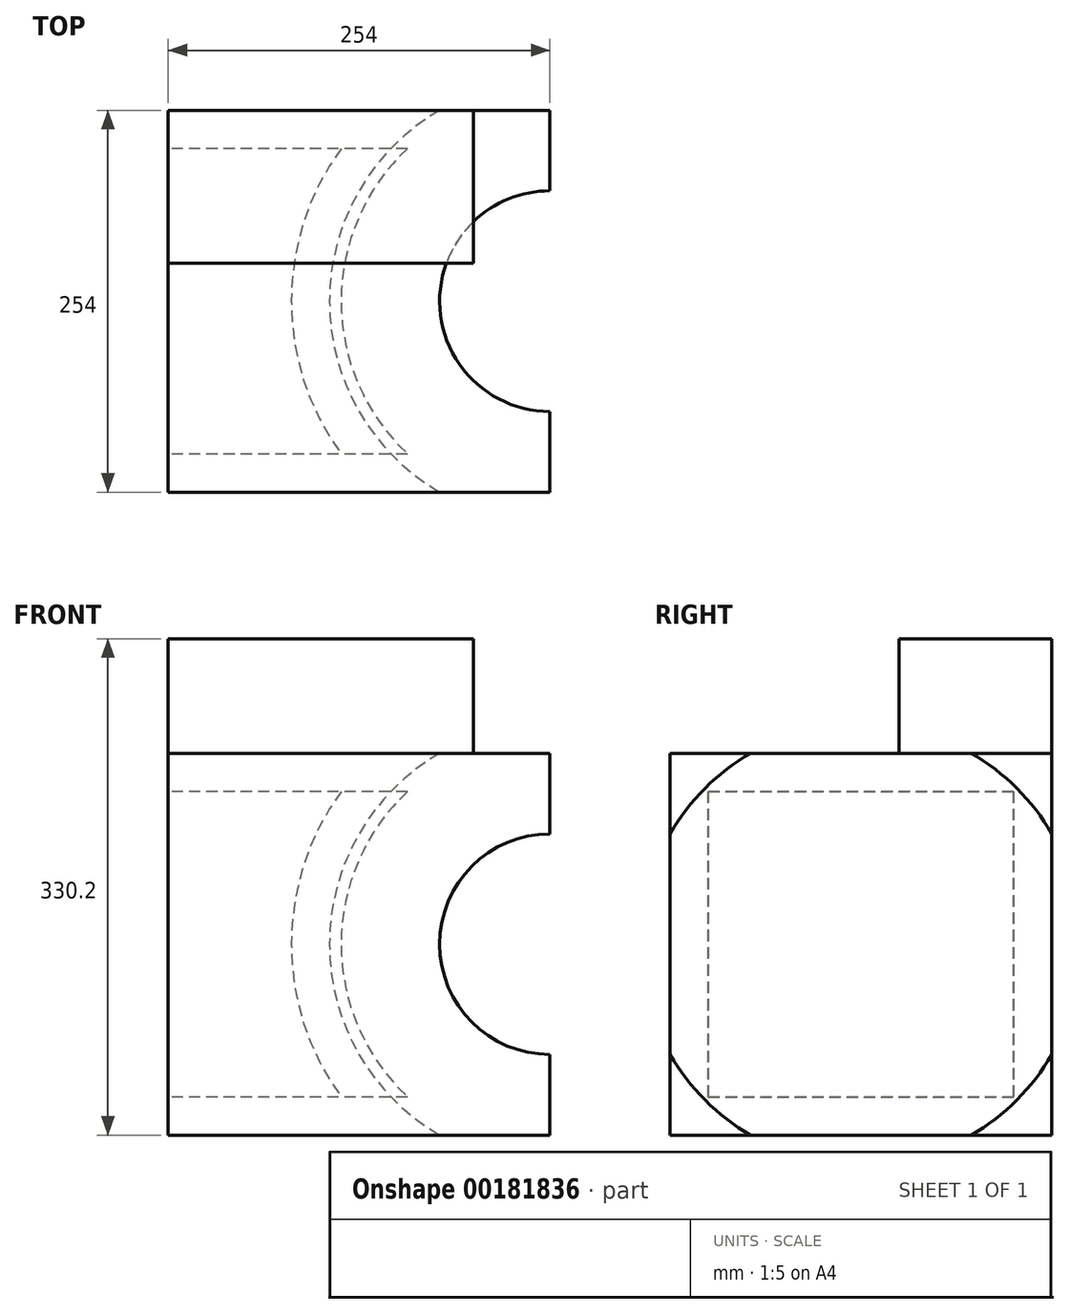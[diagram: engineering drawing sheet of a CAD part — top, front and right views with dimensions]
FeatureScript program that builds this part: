
annotation { "Feature Type Name" : "Feature", "Feature Type Description" : "" }
export const myFeature = defineFeature(function(context is Context, id is Id, definition is map)
    precondition{}
    {
        {
            var Q0;
            Q0=qCreatedBy(makeId("Right.planeOp"),FACE);
            var sketch = newSketch(context, id + "F0", { "sketchPlane" : qUnion([Q0])});
            skLineSegment(sketch, "E0.bottom", {"start": v(-254, 0) * mm, "end": v(0, 0) * mm});
            skLineSegment(sketch, "E0.top", {"start": v(-254, -254) * mm, "end": v(0, -254) * mm});
            skLineSegment(sketch, "E0.left", {"start": v(-254, 0) * mm, "end": v(-254, -254) * mm});
            skLineSegment(sketch, "E0.right", {"start": v(0, 0) * mm, "end": v(0, -254) * mm});
            skSolve(sketch);
        }
        {
            var Q0;
            Q0 = qSketchRegion(id + "F0", true);
            extrude(context, id + "F1", {"entities" : qUnion([Q0]), "depth" : 254 * mm});
        }
        {
            var Q0;
            Q0=makeQuery(id+"F1.opExtrude","CAP_FACE",FACE,{"disambiguationData":[OSD([sQuery(id+"F0.wireOp",EDGE,"E0.bottom"),sQuery(id+"F0.wireOp",EDGE,"E0.top"),sQuery(id+"F0.wireOp",EDGE,"E0.left"),sQuery(id+"F0.wireOp",EDGE,"E0.right")])],"isStart":false});
            var sketch = newSketch(context, id + "F2", { "sketchPlane" : qUnion([Q0])});
            skArc(sketch, "E1", {"start": v(19.67, -127) * mm, "mid": v(-127, 19.67) * mm, "end": v(-273.67, -127) * mm});
            skPoint(sketch, "E1.centerSnap0", {"position": v(-127, -254) * mm});
            skPoint(sketch, "E1.centerSnap1", {"position": v(0, -127) * mm});
            skLineSegment(sketch, "E2", {"start": v(19.67, -127) * mm, "end": v(-273.67, -127) * mm});
            skPoint(sketch, "E2.endSnap0", {"position": v(-254, -127) * mm});
            skSolve(sketch);
        }
        {
            var Q0;
            {var subQ0=sQuery(id+"F2.wireOp",EDGE,"E1");var subQ1=makeQuery(id+"F1.opExtrude","CAP_EDGE",EDGE,{"disambiguationData":[OSD([sQuery(id+"F0.wireOp",EDGE,"E0.bottom")])],"isStart":false});var subQ2=makeQuery(id+"F2.imprint","INTERSECT",VERTEX,{"disambiguationData":[OD(0.0)],"derivedFrom":[subQ1,subQ0]});Q0=makeQuery(id+"F2.imprint","IMPRINT",FACE,{"disambiguationData":[TD([[makeQuery(id+"F2.imprint","IMPRINT",EDGE,{"disambiguationData":[TD([[subQ2,-1.0]])],"derivedFrom":subQ0}),1.0]])]});}
            var Q1;
            {var subQ1=makeQuery(id+"F1.opExtrude","CAP_EDGE",EDGE,{"disambiguationData":[OSD([sQuery(id+"F0.wireOp",EDGE,"E0.right")])],"isStart":false});var subQ5=sQuery(id+"F2.wireOp",EDGE,"E1");var subQ10=makeQuery(id+"F2.imprint","INTERSECT",VERTEX,{"derivedFrom":[subQ1,subQ5]});Q1=makeQuery(id+"F2.imprint","IMPRINT",FACE,{"disambiguationData":[TD([[makeQuery(id+"F2.imprint","IMPRINT",EDGE,{"disambiguationData":[TD([[subQ10,-1.0]])],"derivedFrom":subQ5}),1.0]])]});}
            var Q2;
            {var subQ0=sQuery(id+"F2.wireOp",EDGE,"E2");var subQ1=sQuery(id+"F2.wireOp",EDGE,"E1");var subQ2=makeQuery(id+"F2.imprint","INTERSECT",VERTEX,{"disambiguationData":[OD(0.0)],"derivedFrom":[subQ1,subQ0]});Q2=makeQuery(id+"F2.imprint","IMPRINT",FACE,{"disambiguationData":[TD([[makeQuery(id+"F2.imprint","IMPRINT",EDGE,{"disambiguationData":[TD([[subQ2,-1.0]])],"derivedFrom":subQ1}),1.0]])]});}
            var Q3;
            {var subQ0=sQuery(id+"F2.wireOp",EDGE,"E2");var subQ1=sQuery(id+"F2.wireOp",EDGE,"E1");var subQ2=makeQuery(id+"F2.imprint","INTERSECT",VERTEX,{"disambiguationData":[OD(1.0)],"derivedFrom":[subQ1,subQ0]});Q3=makeQuery(id+"F2.imprint","IMPRINT",FACE,{"disambiguationData":[TD([[makeQuery(id+"F2.imprint","IMPRINT",EDGE,{"disambiguationData":[TD([[subQ2,1.0]])],"derivedFrom":subQ1}),1.0]])]});}
            var Q4;
            Q4=sQuery(id+"F2.wireOp",EDGE,"E2");
            revolve(context, id + "F3", {"operationType" : NewBodyOperationType.REMOVE, "entities" : qUnion([Q0, Q1, Q2, Q3]), "axis" : qUnion([Q4]), "revolveType" : RevolveType.FULL, "oppositeDirection" : true});
        }
        {
            var Q0;
            Q0=makeQuery(id+"F1.opExtrude","CAP_FACE",FACE,{"disambiguationData":[OSD([sQuery(id+"F0.wireOp",EDGE,"E0.bottom"),sQuery(id+"F0.wireOp",EDGE,"E0.top"),sQuery(id+"F0.wireOp",EDGE,"E0.left"),sQuery(id+"F0.wireOp",EDGE,"E0.right")])],"isStart":true});
            shell(context, id + "F4", {"entities" : qUnion([Q0]), "thickness" : 25.4 * mm});
        }
        {
            var Q0;
            Q0=qCreatedBy(makeId("Right.planeOp"),FACE);
            var sketch = newSketch(context, id + "F7", { "sketchPlane" : qUnion([Q0])});
            skLineSegment(sketch, "E3.bottom", {"start": v(-101.6, 76.2) * mm, "end": v(0, 76.2) * mm});
            skLineSegment(sketch, "E3.top", {"start": v(-101.6, 0) * mm, "end": v(0, 0) * mm});
            skLineSegment(sketch, "E3.left", {"start": v(-101.6, 76.2) * mm, "end": v(-101.6, 0) * mm});
            skLineSegment(sketch, "E3.right", {"start": v(0, 76.2) * mm, "end": v(0, 0) * mm});
            skSolve(sketch);
        }
        {
            var Q0;
            Q0 = qSketchRegion(id + "F7", true);
            extrude(context, id + "F5", {"entities" : qUnion([Q0]), "operationType" : NewBodyOperationType.ADD, "depth" : 203.2 * mm});
        }
    });
